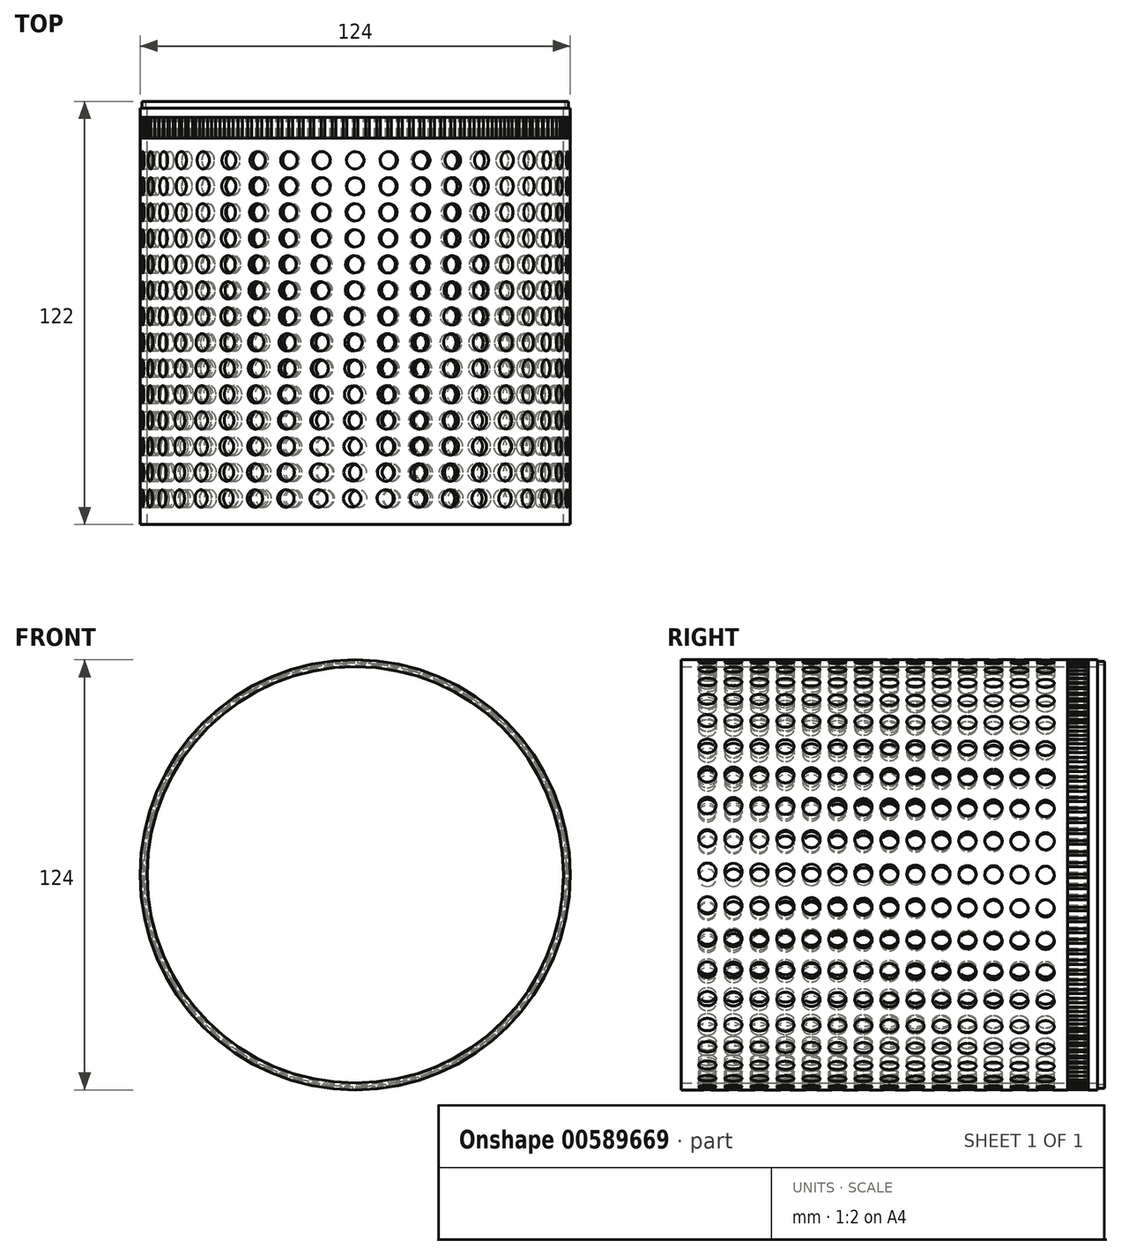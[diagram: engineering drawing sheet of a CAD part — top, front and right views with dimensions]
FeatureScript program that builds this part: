
annotation { "Feature Type Name" : "Feature", "Feature Type Description" : "" }
export const myFeature = defineFeature(function(context is Context, id is Id, definition is map)
    precondition{}
    {
        {
            var Q0;
            Q0=qCreatedBy(makeId("Front.planeOp"),FACE);
            var sketch = newSketch(context, id + "F0", { "sketchPlane" : qUnion([Q0])});
            skCircle(sketch, "E0", {"center": v(0, 0) * mm, "radius": 60 * mm});
            skCircle(sketch, "E1.0", {"center": v(0, 0) * mm, "radius": 62 * mm});
            skSolve(sketch);
        }
        {
            var Q0;
            Q0 = qSketchRegion(id + "F0", true);
            extrude(context, id + "F1", {"entities" : qUnion([Q0]), "depth" : 120 * mm, "offsetDistance" : 25 * mm});
        }
        {
            var Q0;
            Q0=qCreatedBy(makeId("Top.planeOp"),FACE);
            var sketch = newSketch(context, id + "F2", { "sketchPlane" : qUnion([Q0])});
            skCircle(sketch, "E2", {"center": v(0, -15) * mm, "radius": 2.5 * mm});
            skCircle(sketch, "E3.1.0.0", {"center": v(0.07, -22.5) * mm, "radius": 2.5 * mm});
            skCircle(sketch, "E3.2.0.0", {"center": v(0.14, -30) * mm, "radius": 2.5 * mm});
            skCircle(sketch, "E3.3.0.0", {"center": v(0.2, -37.5) * mm, "radius": 2.5 * mm});
            skCircle(sketch, "E3.4.0.0", {"center": v(0.28, -45) * mm, "radius": 2.5 * mm});
            skCircle(sketch, "E3.5.0.0", {"center": v(0.34, -52.5) * mm, "radius": 2.5 * mm});
            skCircle(sketch, "E3.6.0.0", {"center": v(0.41, -60) * mm, "radius": 2.5 * mm});
            skCircle(sketch, "E3.7.0.0", {"center": v(0.48, -67.5) * mm, "radius": 2.5 * mm});
            skCircle(sketch, "E3.8.0.0", {"center": v(0.55, -75) * mm, "radius": 2.5 * mm});
            skCircle(sketch, "E3.9.0.0", {"center": v(0.62, -82.5) * mm, "radius": 2.5 * mm});
            skCircle(sketch, "E3.10.0.0", {"center": v(0.69, -90) * mm, "radius": 2.5 * mm});
            skCircle(sketch, "E3.11.0.0", {"center": v(0.76, -97.5) * mm, "radius": 2.5 * mm});
            skCircle(sketch, "E3.12.0.0", {"center": v(0.83, -105) * mm, "radius": 2.5 * mm});
            skCircle(sketch, "E3.13.0.0", {"center": v(0.9, -112.5) * mm, "radius": 2.5 * mm});
            skLineSegment(sketch, "E3.direction1", {"start": v(0, -15) * mm, "end": v(0.07, -22.5) * mm, "construction": true});
            skSolve(sketch);
        }
        {
            var Q0;
            Q0 = qSketchRegion(id + "F2", true);
            extrude(context, id + "F3", {"entities" : qUnion([Q0]), "operationType" : NewBodyOperationType.REMOVE, "oppositeDirection" : true, "depth" : 210 * mm, "offsetDistance" : 25 * mm});
        }
        {
            var Q0;
            Q0=makeQuery(id+"F3.boolean.opBoolean","COPY",FACE,{"derivedFrom":makeQuery(id+"F3.opExtrude","SWEPT_FACE",FACE,{"disambiguationData":[OSD([sQuery(id+"F2.wireOp",EDGE,"E2")])]})});
            var Q1;
            Q1=makeQuery(id+"F3.boolean.opBoolean","COPY",FACE,{"derivedFrom":makeQuery(id+"F3.opExtrude","SWEPT_FACE",FACE,{"disambiguationData":[OSD([sQuery(id+"F2.wireOp",EDGE,"E3.1.0.0")])]})});
            var Q2;
            Q2=makeQuery(id+"F3.boolean.opBoolean","COPY",FACE,{"derivedFrom":makeQuery(id+"F3.opExtrude","SWEPT_FACE",FACE,{"disambiguationData":[OSD([sQuery(id+"F2.wireOp",EDGE,"E3.2.0.0")])]})});
            var Q3;
            Q3=makeQuery(id+"F3.boolean.opBoolean","COPY",FACE,{"derivedFrom":makeQuery(id+"F3.opExtrude","SWEPT_FACE",FACE,{"disambiguationData":[OSD([sQuery(id+"F2.wireOp",EDGE,"E3.3.0.0")])]})});
            var Q4;
            Q4=makeQuery(id+"F3.boolean.opBoolean","COPY",FACE,{"derivedFrom":makeQuery(id+"F3.opExtrude","SWEPT_FACE",FACE,{"disambiguationData":[OSD([sQuery(id+"F2.wireOp",EDGE,"E3.4.0.0")])]})});
            var Q5;
            Q5=makeQuery(id+"F3.boolean.opBoolean","COPY",FACE,{"derivedFrom":makeQuery(id+"F3.opExtrude","SWEPT_FACE",FACE,{"disambiguationData":[OSD([sQuery(id+"F2.wireOp",EDGE,"E3.5.0.0")])]})});
            var Q6;
            Q6=makeQuery(id+"F3.boolean.opBoolean","COPY",FACE,{"derivedFrom":makeQuery(id+"F3.opExtrude","SWEPT_FACE",FACE,{"disambiguationData":[OSD([sQuery(id+"F2.wireOp",EDGE,"E3.6.0.0")])]})});
            var Q7;
            Q7=makeQuery(id+"F3.boolean.opBoolean","COPY",FACE,{"derivedFrom":makeQuery(id+"F3.opExtrude","SWEPT_FACE",FACE,{"disambiguationData":[OSD([sQuery(id+"F2.wireOp",EDGE,"E3.7.0.0")])]})});
            var Q8;
            Q8=makeQuery(id+"F3.boolean.opBoolean","COPY",FACE,{"derivedFrom":makeQuery(id+"F3.opExtrude","SWEPT_FACE",FACE,{"disambiguationData":[OSD([sQuery(id+"F2.wireOp",EDGE,"E3.8.0.0")])]})});
            var Q9;
            Q9=makeQuery(id+"F3.boolean.opBoolean","COPY",FACE,{"derivedFrom":makeQuery(id+"F3.opExtrude","SWEPT_FACE",FACE,{"disambiguationData":[OSD([sQuery(id+"F2.wireOp",EDGE,"E3.9.0.0")])]})});
            var Q10;
            Q10=makeQuery(id+"F3.boolean.opBoolean","COPY",FACE,{"derivedFrom":makeQuery(id+"F3.opExtrude","SWEPT_FACE",FACE,{"disambiguationData":[OSD([sQuery(id+"F2.wireOp",EDGE,"E3.10.0.0")])]})});
            var Q11;
            Q11=makeQuery(id+"F3.boolean.opBoolean","COPY",FACE,{"derivedFrom":makeQuery(id+"F3.opExtrude","SWEPT_FACE",FACE,{"disambiguationData":[OSD([sQuery(id+"F2.wireOp",EDGE,"E3.11.0.0")])]})});
            var Q12;
            Q12=makeQuery(id+"F3.boolean.opBoolean","COPY",FACE,{"derivedFrom":makeQuery(id+"F3.opExtrude","SWEPT_FACE",FACE,{"disambiguationData":[OSD([sQuery(id+"F2.wireOp",EDGE,"E3.12.0.0")])]})});
            var Q13;
            Q13=makeQuery(id+"F3.boolean.opBoolean","COPY",FACE,{"derivedFrom":makeQuery(id+"F3.opExtrude","SWEPT_FACE",FACE,{"disambiguationData":[OSD([sQuery(id+"F2.wireOp",EDGE,"E3.13.0.0")])]})});
            var Q14;
            Q14=makeQuery(id+"F3.boolean.opBoolean","COPY",FACE,{"derivedFrom":makeQuery(id+"F3.opExtrude","SWEPT_FACE",FACE,{"disambiguationData":[OSD([sQuery(id+"F2.wireOp",EDGE,"E3.14.0.0")])]})});
            var Q15;
            Q15=makeQuery(id+"F1.opExtrude","CAP_EDGE",EDGE,{"disambiguationData":[OSD([sQuery(id+"F0.wireOp",EDGE,"E0")])],"isStart":false});
            circularPattern(context, id + "F4", {"patternType" : PatternType.FACE, "operationType" : NewBodyOperationType.REMOVE, "faces" : qUnion([Q0, Q1, Q2, Q3, Q4, Q5, Q6, Q7, Q8, Q9, Q10, Q11, Q12, Q13, Q14]), "axis" : qUnion([Q15]), "angle" : 360 * degree, "instanceCount" : 40, "equalSpace" : true});
        }
        {
            var Q0;
            Q0=qCreatedBy(makeId("Top.planeOp"),FACE);
            var sketch = newSketch(context, id + "F5", { "sketchPlane" : qUnion([Q0])});
            skLineSegment(sketch, "E4", {"start": v(-62, -120) * mm, "end": v(-62, -1.96) * mm});
            skLineSegment(sketch, "E5", {"start": v(-62, -2.64) * mm, "end": v(-61, -2.64) * mm});
            skLineSegment(sketch, "E6", {"start": v(-61, -2.64) * mm, "end": v(-61, -8.64) * mm});
            skLineSegment(sketch, "E7", {"start": v(-61, -8.64) * mm, "end": v(-62, -8.64) * mm});
            skSolve(sketch);
        }
        {
            var Q0;
            Q0 = qSketchRegion(id + "F5", true);
            var Q1;
            Q1=makeQuery(id+"F1.opExtrude","CAP_EDGE",EDGE,{"disambiguationData":[OSD([sQuery(id+"F0.wireOp",EDGE,"E1.0")])],"isStart":true});
            revolve(context, id + "F6", {"operationType" : NewBodyOperationType.REMOVE, "entities" : qUnion([Q0]), "axis" : qUnion([Q1]), "revolveType" : RevolveType.FULL, "oppositeDirection" : true});
        }
        {
            var Q0;
            Q0=makeQuery(id+"F6.boolean.opBoolean","COPY",FACE,{"derivedFrom":makeQuery(id+"F6.opRevolve","SWEPT_FACE",FACE,{"disambiguationData":[OSD([sQuery(id+"F5.wireOp",EDGE,"E5")])]})});
            var sketch = newSketch(context, id + "F7", { "sketchPlane" : qUnion([Q0])});
            skLineSegment(sketch, "E8", {"start": v(0.3, 0) * mm, "end": v(0.3, 87.88) * mm, "construction": true});
            skArc(sketch, "E9.0", {"start": v(0.8, 61) * mm, "mid": v(0.3, 61) * mm, "end": v(-0.2, 61) * mm});
            skLineSegment(sketch, "E10", {"start": v(0.8, 61) * mm, "end": v(0.8, 61.58) * mm});
            skLineSegment(sketch, "E11", {"start": v(0.4, 61.98) * mm, "end": v(0.2, 61.98) * mm});
            skLineSegment(sketch, "E12", {"start": v(-0.2, 61.58) * mm, "end": v(-0.2, 61) * mm});
            skPoint(sketch, "E13.visualSharp", {"position": v(-0.2, 61.98) * mm});
            skArc(sketch, "E13.filletArc", {"start": v(0.2, 61.98) * mm, "mid": v(-0.1, 61.86) * mm, "end": v(-0.2, 61.58) * mm});
            skPoint(sketch, "E14.visualSharp", {"position": v(0.8, 61.98) * mm});
            skArc(sketch, "E14.filletArc", {"start": v(0.8, 61.58) * mm, "mid": v(0.67, 61.86) * mm, "end": v(0.4, 61.98) * mm});
            skLineSegment(sketch, "E15", {"start": v(-0.2, 61.48) * mm, "end": v(-2.45, 61.4) * mm, "construction": true});
            skCircle(sketch, "E16", {"center": v(0.3, 0) * mm, "radius": 60.94 * mm, "construction": true});
            skSolve(sketch);
        }
        {
            var Q0;
            Q0=makeQuery(id+"F1.opExtrude","CAP_FACE",FACE,{"disambiguationData":[OSD([sQuery(id+"F0.wireOp",EDGE,"E0"),sQuery(id+"F0.wireOp",EDGE,"E1.0")])],"isStart":true});
            var sketch = newSketch(context, id + "F8", { "sketchPlane" : qUnion([Q0])});
            skCircle(sketch, "E17", {"center": v(0, 0) * mm, "radius": 60.5 * mm});
            skCircle(sketch, "E18.0", {"center": v(0, 0) * mm, "radius": 61.5 * mm});
            skSolve(sketch);
        }
        {
            var Q0;
            Q0 = qSketchRegion(id + "F8", true);
            extrude(context, id + "F9", {"entities" : qUnion([Q0]), "operationType" : NewBodyOperationType.ADD, "depth" : 2 * mm, "offsetDistance" : 25 * mm});
        }
        {
            var Q0;
            Q0 = qSketchRegion(id + "F7", true);
            extrude(context, id + "F10", {"entities" : qUnion([Q0]), "operationType" : NewBodyOperationType.ADD, "depth" : 6 * mm, "offsetDistance" : 25 * mm});
        }
        {
            var Q0;
            Q0 = qSketchRegion(id + "F7", true);
            extrude(context, id + "F11", {"entities" : qUnion([Q0]), "operationType" : NewBodyOperationType.ADD, "depth" : 6 * mm, "offsetDistance" : 25 * mm});
        }
        {
            var Q0;
            Q0=makeQuery(id+"F10.opExtrude","SWEPT_FACE",FACE,{"disambiguationData":[OSD([sQuery(id+"F7.wireOp",EDGE,"E12")])]});
            var Q1;
            Q1=makeQuery(id+"F10.opExtrude","SWEPT_FACE",FACE,{"disambiguationData":[OSD([sQuery(id+"F7.wireOp",EDGE,"E13.filletArc")])]});
            var Q2;
            Q2=makeQuery(id+"F10.opExtrude","SWEPT_FACE",FACE,{"disambiguationData":[OSD([sQuery(id+"F7.wireOp",EDGE,"E11")])]});
            var Q3;
            Q3=makeQuery(id+"F10.opExtrude","SWEPT_FACE",FACE,{"disambiguationData":[OSD([sQuery(id+"F7.wireOp",EDGE,"E14.filletArc")])]});
            var Q4;
            Q4=makeQuery(id+"F10.opExtrude","SWEPT_FACE",FACE,{"disambiguationData":[OSD([sQuery(id+"F7.wireOp",EDGE,"E10")])]});
            var Q5;
            Q5=makeQuery(id+"F9.opExtrude","CAP_EDGE",EDGE,{"disambiguationData":[OSD([sQuery(id+"F8.wireOp",EDGE,"E18.0")])],"isStart":false});
            circularPattern(context, id + "F12", {"patternType" : PatternType.FACE, "faces" : qUnion([Q0, Q1, Q2, Q3, Q4]), "axis" : qUnion([Q5]), "angle" : 360 * degree, "instanceCount" : 120, "equalSpace" : true});
        }
    });
